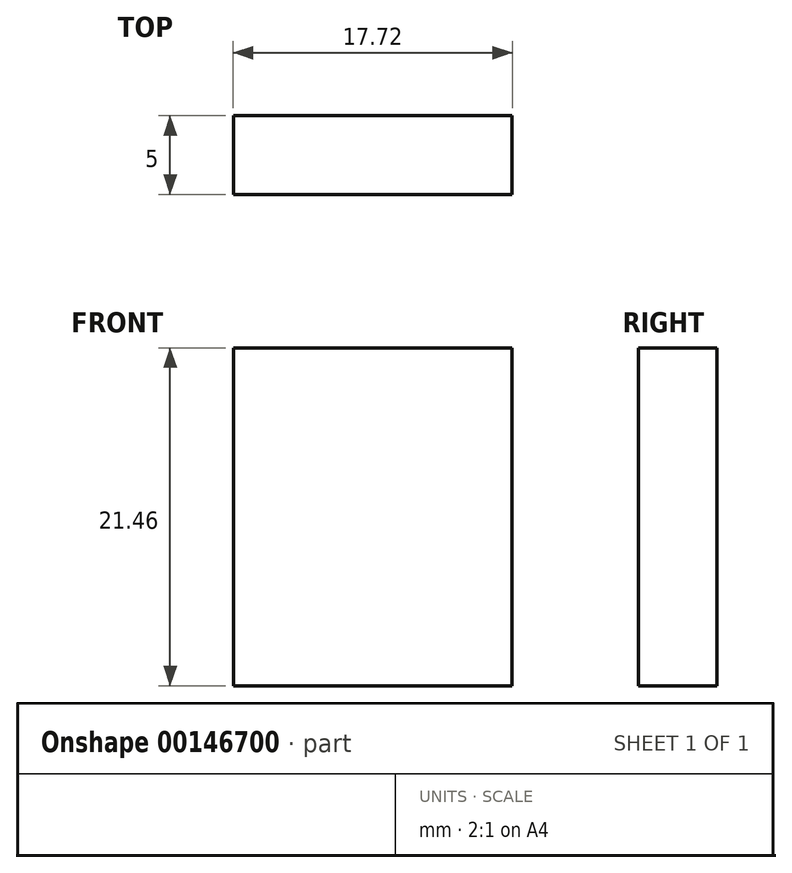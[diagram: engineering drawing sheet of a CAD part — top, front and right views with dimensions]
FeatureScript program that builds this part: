
annotation { "Feature Type Name" : "Feature", "Feature Type Description" : "" }
export const myFeature = defineFeature(function(context is Context, id is Id, definition is map)
    precondition{}
    {
        {
            var Q0;
            Q0=qCreatedBy(makeId("Front.planeOp"),FACE);
            var sketch = newSketch(context, id + "F0", { "sketchPlane" : qUnion([Q0])});
            skLineSegment(sketch, "E0.bottom", {"start": v(8.86, -10.73) * mm, "end": v(-8.86, -10.73) * mm});
            skLineSegment(sketch, "E0.top", {"start": v(8.86, 10.73) * mm, "end": v(-8.86, 10.73) * mm});
            skLineSegment(sketch, "E0.left", {"start": v(8.86, -10.73) * mm, "end": v(8.86, 10.73) * mm});
            skLineSegment(sketch, "E0.right", {"start": v(-8.86, -10.73) * mm, "end": v(-8.86, 10.73) * mm});
            skPoint(sketch, "E0.middle", {"position": v(0, 0) * mm});
            skSolve(sketch);
        }
        {
            var Q0;
            Q0=makeQuery(id+"F0.imprint","IMPRINT",FACE,{"disambiguationData":[TD([[makeQuery(id+"F0.imprint","IMPRINT",EDGE,{"derivedFrom":sQuery(id+"F0.wireOp",EDGE,"E0.bottom")}),-1.0]])]});
            extrude(context, id + "F1", {"entities" : qUnion([Q0]), "depth" : 5 * mm});
        }
    });
